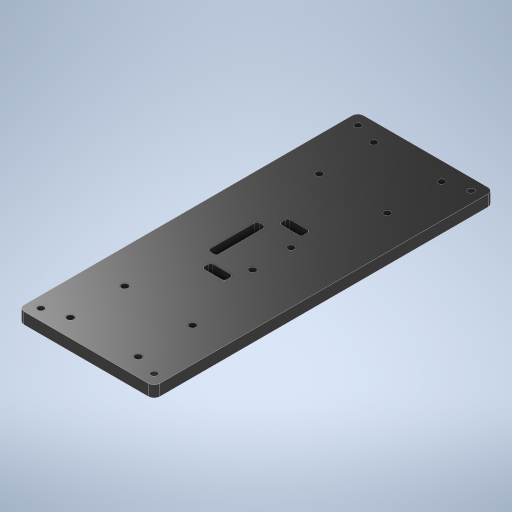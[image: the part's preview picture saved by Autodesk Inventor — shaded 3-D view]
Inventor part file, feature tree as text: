
AUTODESK INVENTOR PART (.ipt)
format: ipt  version: 2023 (Build 270158000, 158)  size: 356,864 bytes
history: native  units: in
note: dims shown in document units (in); Inventor stores cm internally (conversion verified against a paired STEP export)
features: fillet x4, extrude x2, sketch x1
ambient origin geometry x8: Origin, YZ Plane, XZ Plane, XY Plane, X Axis, Y Axis, Z Axis, Center Point
bodies: Solid1 (feature_tree)
feature tree (7):
  sketch  "Sketch1"  dims[d0=2.3622in d1=5.9055in d2=0.1969in d3=0.1969in d4=0.1969in d5=0.1969in d6=0.1969in d7=0.1969in d8=0.1969in d9=0.1969in d10=0.1102in d11=0.1102in d39=0.7492in d40=0.8681in d41=0.0984in d42=0.0984in d43=0.0984in d44=0.0984in d45=0.1181in d46=0.1181in d47=0.0394in d48=0.1575in d49=0.1969in d50=0.0in d51=0.0984in d52=0.0394in d53=0.0394in d54=0.7874in d55=1.5748in d56=0.7874in d57=0.7874in d58=1.5748in d59=0.7874in d60=0.315in d61=0.315in d62=0.1969in d63=1.1811in d64=0.9449in d65=0.9449in d66=0.1181in d67=0.1181in d68=0.1181in d69=0.1181in d70=0.1181in d71=0.1181in d72=0.1181in d73=0.1969in d74=0.0in d75=0.6299in d76=0.6299in d77=0.1969in d78=0.1575in d79=0.1969in d80=0.1969in d81=0.1575in d82=0.1969in d83=0.0394in]
  extrude  "Extrusion1"  Depth=5.9055in
  fillet  "Fillet1"  Radius=0.1969in
  fillet  "Fillet2"  Radius=0.1969in
  fillet  "Fillet3"  Radius=0.1969in
  extrude  "Extrusion2"  Depth=0.1969in
  fillet  "Fillet4"  Radius=0.1969in
